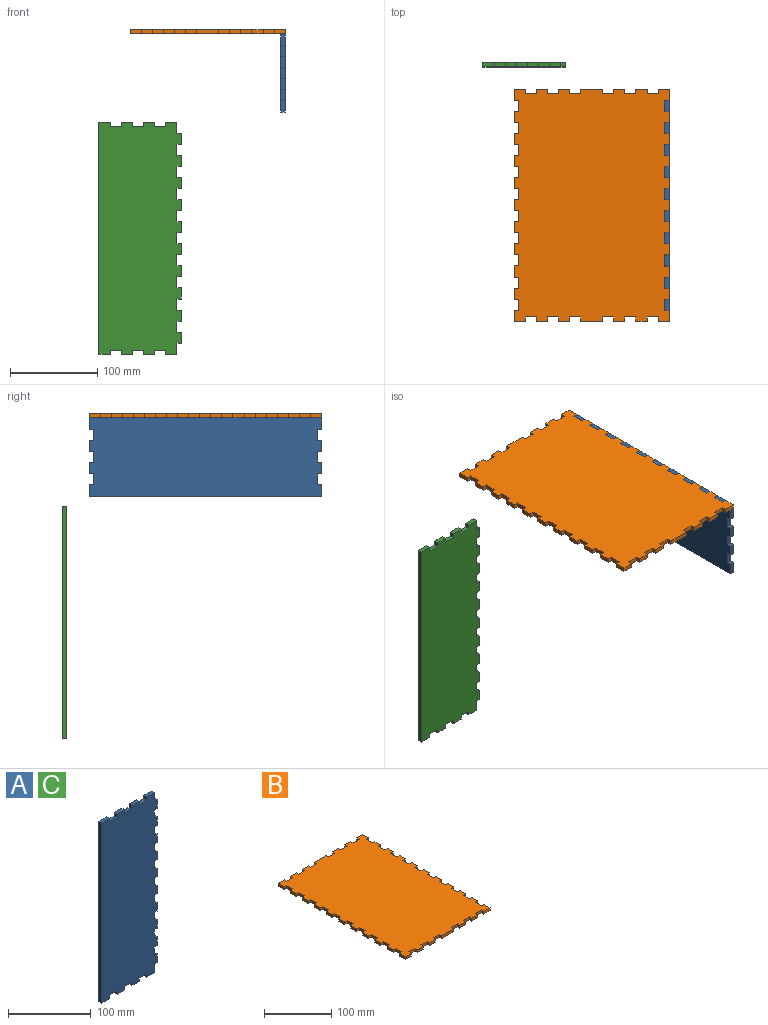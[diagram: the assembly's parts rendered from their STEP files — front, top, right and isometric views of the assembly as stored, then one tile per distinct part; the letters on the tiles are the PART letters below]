
ASSEMBLY  parts=3 mates=1
PART A: 70 faces, bbox 94.7x5x266.9 mm
  f0: plane 5x5mm, normal (0,0,-1), area 25mm2, adj f1,f67,f68,f69
  f1: plane 12.7x5mm, normal (1,0,0), area 63.5mm2, adj f0,f2,f68,f69
  f2: plane 5x5mm, normal (0,0,1), area 25mm2, adj f1,f3,f68,f69
  f3: plane 12.7x5mm, normal (1,0,0), area 63.5mm2, adj f2,f4,f68,f69
  f4: plane 5x5mm, normal (0,0,-1), area 25mm2, adj f3,f5,f68,f69
  f5: plane 12.7x5mm, normal (1,0,0), area 63.5mm2, adj f4,f6,f68,f69
  f6: plane 5x5mm, normal (0,0,1), area 25mm2, adj f5,f7,f68,f69
  f7: plane 12.7x5mm, normal (1,0,0), area 63.5mm2, adj f6,f8,f68,f69
  f8: plane 5x5mm, normal (0,0,-1), area 25mm2, adj f7,f9,f68,f69
  f9: plane 12.7x5mm, normal (1,0,0), area 63.5mm2, adj f8,f10,f68,f69
  f10: plane 5x5mm, normal (0,0,1), area 25mm2, adj f9,f11,f68,f69
  f11: plane 12.7x5mm, normal (1,0,0), area 63.5mm2, adj f10,f12,f68,f69
  f12: plane 5x5mm, normal (0,0,-1), area 25mm2, adj f11,f13,f68,f69
  f13: plane 12.7x5mm, normal (1,0,0), area 63.5mm2, adj f12,f14,f68,f69
  f14: plane 5x5mm, normal (0,0,1), area 25mm2, adj f13,f15,f68,f69
  f15: plane 12.7x5mm, normal (1,0,0), area 63.5mm2, adj f14,f16,f68,f69
  f16: plane 5x5mm, normal (0,0,-1), area 25mm2, adj f15,f17,f68,f69
  f17: plane 12.7x5mm, normal (1,0,0), area 63.5mm2, adj f16,f18,f68,f69
  f18: plane 5x5mm, normal (0,0,1), area 25mm2, adj f17,f19,f68,f69
  f19: plane 12.7x5mm, normal (1,0,0), area 63.5mm2, adj f18,f20,f68,f69
  f20: plane 5x5mm, normal (0,0,-1), area 25mm2, adj f19,f21,f68,f69
  f21: plane 12.8x5mm, normal (1,0,0), area 64mm2, adj f20,f22,f68,f69
  f22: plane 5x5mm, normal (0,0,1), area 25mm2, adj f21,f23,f68,f69
  f23: plane 12.7x5mm, normal (1,0,0), area 63.5mm2, adj f22,f24,f68,f69
  f24: plane 12.7x5mm, normal (0,0,1), area 63.5mm2, adj f23,f25,f68,f69
  f25: plane 5x5mm, normal (-1,0,0), area 25mm2, adj f24,f26,f68,f69
  f26: plane 12.7x5mm, normal (0,0,1), area 63.5mm2, adj f25,f27,f68,f69
  f27: plane 5x5mm, normal (1,0,0), area 25mm2, adj f26,f28,f68,f69
  f28: plane 12.7x5mm, normal (0,0,1), area 63.5mm2, adj f27,f29,f68,f69
  f29: plane 5x5mm, normal (-1,0,0), area 25mm2, adj f28,f30,f68,f69
  f30: plane 12.7x5mm, normal (0,0,1), area 63.5mm2, adj f29,f31,f68,f69
  f31: plane 5x5mm, normal (1,0,0), area 25mm2, adj f30,f32,f68,f69
  f32: plane 12.7x5mm, normal (0,0,1), area 63.5mm2, adj f31,f33,f68,f69
  f33: plane 5x5mm, normal (-1,0,0), area 25mm2, adj f32,f34,f68,f69
  f34: plane 12.7x5mm, normal (0,0,1), area 63.5mm2, adj f33,f35,f68,f69
  f35: plane 5x5mm, normal (1,0,0), area 25mm2, adj f34,f36,f68,f69
  f36: plane 13.49x5mm, normal (0,0,1), area 67.4mm2, adj f35,f37,f68,f69
  f37: plane 266.9x5mm, normal (-1,0,0), area 1334.5mm2, adj f36,f38,f68,f69
  f38: plane 13.49x5mm, normal (0,0,-1), area 67.4mm2, adj f37,f39,f68,f69
  f39: plane 5x5mm, normal (1,0,0), area 25mm2, adj f38,f40,f68,f69
  f40: plane 12.7x5mm, normal (0,0,-1), area 63.5mm2, adj f39,f41,f68,f69
  f41: plane 5x5mm, normal (-1,0,0), area 25mm2, adj f40,f42,f68,f69
  f42: plane 12.7x5mm, normal (0,0,-1), area 63.5mm2, adj f41,f43,f68,f69
  f43: plane 5x5mm, normal (1,0,0), area 25mm2, adj f42,f44,f68,f69
  f44: plane 12.7x5mm, normal (0,0,-1), area 63.5mm2, adj f43,f45,f68,f69
  f45: plane 5x5mm, normal (-1,0,0), area 25mm2, adj f44,f46,f68,f69
  f46: plane 12.7x5mm, normal (0,0,-1), area 63.5mm2, adj f45,f47,f68,f69
  f47: plane 5x5mm, normal (1,0,0), area 25mm2, adj f46,f48,f68,f69
  f48: plane 12.7x5mm, normal (0,0,-1), area 63.5mm2, adj f47,f49,f68,f69
  f49: plane 5x5mm, normal (-1,0,0), area 25mm2, adj f48,f50,f68,f69
  f50: plane 12.7x5mm, normal (0,0,-1), area 63.5mm2, adj f49,f51,f68,f69
  f51: plane 12.7x5mm, normal (1,0,0), area 63.5mm2, adj f50,f52,f68,f69
  f52: plane 5x5mm, normal (0,0,-1), area 25mm2, adj f51,f53,f68,f69
  f53: plane 12.8x5mm, normal (1,0,0), area 64mm2, adj f52,f54,f68,f69
  f54: plane 5x5mm, normal (0,0,1), area 25mm2, adj f53,f55,f68,f69
  f55: plane 12.7x5mm, normal (1,0,0), area 63.5mm2, adj f54,f56,f68,f69
  f56: plane 5x5mm, normal (0,0,-1), area 25mm2, adj f55,f57,f68,f69
  f57: plane 12.7x5mm, normal (1,0,0), area 63.5mm2, adj f56,f58,f68,f69
  f58: plane 5x5mm, normal (0,0,1), area 25mm2, adj f57,f59,f68,f69
  f59: plane 12.7x5mm, normal (1,0,0), area 63.5mm2, adj f58,f60,f68,f69
  f60: plane 5x5mm, normal (0,0,-1), area 25mm2, adj f59,f61,f68,f69
  f61: plane 12.7x5mm, normal (1,0,0), area 63.5mm2, adj f60,f62,f68,f69
  f62: plane 5x5mm, normal (0,0,1), area 25mm2, adj f61,f63,f68,f69
  f63: plane 12.7x5mm, normal (1,0,0), area 63.5mm2, adj f62,f64,f68,f69
  f64: plane 5x5mm, normal (0,0,-1), area 25mm2, adj f63,f65,f68,f69
  f65: plane 12.7x5mm, normal (1,0,0), area 63.5mm2, adj f64,f66,f68,f69
  f66: plane 5x5mm, normal (0,0,1), area 25mm2, adj f65,f67,f68,f69
  f67: plane 12.7x5mm, normal (1,0,0), area 63.5mm2, adj f0,f66,f68,f69
  f68: plane 266.9x94.69mm, normal (0,-1,0), area 24192.3mm2, adj f0,f1,f2,f3,f4,f5,f6,f7
  f69: plane 266.9x94.69mm, normal (0,1,0), area 24192.3mm2, adj f0,f1,f2,f3,f4,f5,f6,f7
PART B: 134 faces, bbox 177.8x266.7x5 mm
  f0: plane 12.7x5mm, normal (0,1,0), area 63.5mm2, adj f1,f131,f132,f133
  f1: plane 5x4.89mm, normal (1,0,0), area 24.4mm2, adj f0,f2,f132,f133
  f2: plane 12.7x5mm, normal (0.01,1,0), area 63.5mm2, adj f1,f3,f132,f133
  f3: plane 5x5mm, normal (-1,0,0), area 25mm2, adj f2,f4,f132,f133
  f4: plane 12.7x5mm, normal (0,1,0), area 63.5mm2, adj f3,f5,f132,f133
  f5: plane 5x5mm, normal (1,0,0), area 25mm2, adj f4,f6,f132,f133
  f6: plane 12.7x5mm, normal (0,1,0), area 63.5mm2, adj f5,f7,f132,f133
  f7: plane 12.7x5mm, normal (-1,0,0), area 63.5mm2, adj f6,f8,f132,f133
  f8: plane 5x5mm, normal (0,-1,0), area 25mm2, adj f7,f9,f132,f133
  f9: plane 12.7x5mm, normal (-1,0,0), area 63.5mm2, adj f8,f10,f132,f133
  f10: plane 5x5mm, normal (0,1,0), area 25mm2, adj f9,f11,f132,f133
  f11: plane 12.7x5mm, normal (-1,0,0), area 63.5mm2, adj f10,f12,f132,f133
  f12: plane 5x5mm, normal (0,-1,0), area 25mm2, adj f11,f13,f132,f133
  f13: plane 12.7x5mm, normal (-1,0,0), area 63.5mm2, adj f12,f14,f132,f133
  f14: plane 5x5mm, normal (0,1,0), area 25mm2, adj f13,f15,f132,f133
  f15: plane 12.7x5mm, normal (-1,0,0), area 63.5mm2, adj f14,f16,f132,f133
  f16: plane 5x5mm, normal (0,-1,0), area 25mm2, adj f15,f17,f132,f133
  f17: plane 12.7x5mm, normal (-1,0,0), area 63.5mm2, adj f16,f18,f132,f133
  f18: plane 5x5mm, normal (0,1,0), area 25mm2, adj f17,f19,f132,f133
  f19: plane 12.7x5mm, normal (-1,0,0), area 63.5mm2, adj f18,f20,f132,f133
  f20: plane 5x5mm, normal (0,-1,0), area 25mm2, adj f19,f21,f132,f133
  f21: plane 12.7x5mm, normal (-1,0,0), area 63.5mm2, adj f20,f22,f132,f133
  f22: plane 5x5mm, normal (0,1,0), area 25mm2, adj f21,f23,f132,f133
  f23: plane 12.7x5mm, normal (-1,0,0), area 63.5mm2, adj f22,f24,f132,f133
  f24: plane 5x5mm, normal (0,-1,0), area 25mm2, adj f23,f25,f132,f133
  f25: plane 12.7x5mm, normal (-1,0,0), area 63.5mm2, adj f24,f26,f132,f133
  f26: plane 5x5mm, normal (0,1,0), area 25mm2, adj f25,f27,f132,f133
  f27: plane 12.7x5mm, normal (-1,0,0), area 63.5mm2, adj f26,f28,f132,f133
  f28: plane 5x5mm, normal (0,-1,0), area 25mm2, adj f27,f29,f132,f133
  f29: plane 12.7x5mm, normal (-1,0,0), area 63.5mm2, adj f28,f30,f132,f133
  f30: plane 5x5mm, normal (0,1,0), area 25mm2, adj f29,f31,f132,f133
  f31: plane 12.7x5mm, normal (-1,0,0), area 63.5mm2, adj f30,f32,f132,f133
  f32: plane 5x5mm, normal (0,-1,0), area 25mm2, adj f31,f33,f132,f133
  f33: plane 12.7x5mm, normal (-1,0,0), area 63.5mm2, adj f32,f34,f132,f133
  f34: plane 5x5mm, normal (0,1,0), area 25mm2, adj f33,f35,f132,f133
  f35: plane 12.7x5mm, normal (-1,0,0), area 63.5mm2, adj f34,f36,f132,f133
  f36: plane 5x5mm, normal (0,-1,0), area 25mm2, adj f35,f37,f132,f133
  f37: plane 12.7x5mm, normal (-1,0,0), area 63.5mm2, adj f36,f38,f132,f133
  f38: plane 5x5mm, normal (0,1,0), area 25mm2, adj f37,f39,f132,f133
  f39: plane 12.7x5mm, normal (-1,0,0), area 63.5mm2, adj f38,f40,f132,f133
  f40: plane 5x5mm, normal (0,-1,0), area 25mm2, adj f39,f41,f132,f133
  f41: plane 12.7x5mm, normal (-1,0,0), area 63.5mm2, adj f40,f42,f132,f133
  f42: plane 5x5mm, normal (0,1,0), area 25mm2, adj f41,f43,f132,f133
  f43: plane 12.7x5mm, normal (-1,0,0), area 63.5mm2, adj f42,f44,f132,f133
  f44: plane 5x5mm, normal (0,-1,0), area 25mm2, adj f43,f45,f132,f133
  f45: plane 12.7x5mm, normal (-1,0,0), area 63.5mm2, adj f44,f46,f132,f133
  f46: plane 5x5mm, normal (0,1,0), area 25mm2, adj f45,f47,f132,f133
  f47: plane 12.7x5mm, normal (-1,0,0), area 63.5mm2, adj f46,f48,f132,f133
  f48: plane 12.7x5mm, normal (0,-1,0), area 63.5mm2, adj f47,f49,f132,f133
  f49: plane 5x5mm, normal (1,0,0), area 25mm2, adj f48,f50,f132,f133
  f50: plane 12.7x5mm, normal (0,-1,0), area 63.5mm2, adj f49,f51,f132,f133
  f51: plane 5x5mm, normal (-1,0,0), area 25mm2, adj f50,f52,f132,f133
  f52: plane 12.7x5mm, normal (0.01,-1,0), area 63.5mm2, adj f51,f53,f132,f133
  f53: plane 5x4.89mm, normal (1,0,0), area 24.4mm2, adj f52,f54,f132,f133
  f54: plane 12.7x5mm, normal (0,-1,0), area 63.5mm2, adj f53,f55,f132,f133
  f55: plane 5x5mm, normal (-1,0,0), area 25mm2, adj f54,f56,f132,f133
  f56: plane 12.7x5mm, normal (0,-1,0), area 63.5mm2, adj f55,f57,f132,f133
  f57: plane 5x5mm, normal (1,0,0), area 25mm2, adj f56,f58,f132,f133
  f58: plane 12.7x5mm, normal (0,-1,0), area 63.5mm2, adj f57,f59,f132,f133
  f59: plane 5x5mm, normal (-1,0,0), area 25mm2, adj f58,f60,f132,f133
  f60: plane 25.4x5mm, normal (0,-1,0), area 127mm2, adj f59,f61,f132,f133
  f61: plane 5x5mm, normal (1,0,0), area 25mm2, adj f60,f62,f132,f133
  f62: plane 12.7x5mm, normal (0,-1,0), area 63.5mm2, adj f61,f63,f132,f133
  f63: plane 5x5mm, normal (-1,0,0), area 25mm2, adj f62,f64,f132,f133
  f64: plane 12.7x5mm, normal (0,-1,0), area 63.5mm2, adj f63,f65,f132,f133
  f65: plane 5x5mm, normal (1,0,0), area 25mm2, adj f64,f66,f132,f133
  f66: plane 12.7x5mm, normal (0,-1,0), area 63.5mm2, adj f65,f67,f132,f133
  f67: plane 5x4.89mm, normal (-1,0,0), area 24.4mm2, adj f66,f68,f132,f133
  f68: plane 12.7x5mm, normal (-0.01,-1,0), area 63.5mm2, adj f67,f69,f132,f133
  f69: plane 5x5mm, normal (1,0,0), area 25mm2, adj f68,f70,f132,f133
  f70: plane 12.7x5mm, normal (0,-1,0), area 63.5mm2, adj f69,f71,f132,f133
  f71: plane 5x5mm, normal (-1,0,0), area 25mm2, adj f70,f72,f132,f133
  f72: plane 12.7x5mm, normal (0,-1,0), area 63.5mm2, adj f71,f73,f132,f133
  f73: plane 12.7x5mm, normal (1,0,0), area 63.5mm2, adj f72,f74,f132,f133
  f74: plane 5x5mm, normal (0,1,0), area 25mm2, adj f73,f75,f132,f133
  f75: plane 12.7x5mm, normal (1,0,0), area 63.5mm2, adj f74,f76,f132,f133
  f76: plane 5x5mm, normal (0,-1,0), area 25mm2, adj f75,f77,f132,f133
  f77: plane 12.7x5mm, normal (1,0,0), area 63.5mm2, adj f76,f78,f132,f133
  f78: plane 5x5mm, normal (0,1,0), area 25mm2, adj f77,f79,f132,f133
  f79: plane 12.7x5mm, normal (1,0,0), area 63.5mm2, adj f78,f80,f132,f133
  f80: plane 5x5mm, normal (0,-1,0), area 25mm2, adj f79,f81,f132,f133
  f81: plane 12.7x5mm, normal (1,0,0), area 63.5mm2, adj f80,f82,f132,f133
  f82: plane 5x5mm, normal (0,1,0), area 25mm2, adj f81,f83,f132,f133
  f83: plane 12.7x5mm, normal (1,0,0), area 63.5mm2, adj f82,f84,f132,f133
  f84: plane 5x5mm, normal (0,-1,0), area 25mm2, adj f83,f85,f132,f133
  f85: plane 12.7x5mm, normal (1,0,0), area 63.5mm2, adj f84,f86,f132,f133
  f86: plane 5x5mm, normal (0,1,0), area 25mm2, adj f85,f87,f132,f133
  f87: plane 12.7x5mm, normal (1,0,0), area 63.5mm2, adj f86,f88,f132,f133
  f88: plane 5x5mm, normal (0,-1,0), area 25mm2, adj f87,f89,f132,f133
  f89: plane 12.7x5mm, normal (1,0,0), area 63.5mm2, adj f88,f90,f132,f133
  f90: plane 5x5mm, normal (0,1,0), area 25mm2, adj f89,f91,f132,f133
  f91: plane 12.7x5mm, normal (1,0,0), area 63.5mm2, adj f90,f92,f132,f133
  f92: plane 5x5mm, normal (0,-1,0), area 25mm2, adj f91,f93,f132,f133
  f93: plane 12.7x5mm, normal (1,0,0), area 63.5mm2, adj f92,f94,f132,f133
  f94: plane 5x5mm, normal (0,1,0), area 25mm2, adj f93,f95,f132,f133
  f95: plane 12.7x5mm, normal (1,0,0), area 63.5mm2, adj f94,f96,f132,f133
  f96: plane 5x5mm, normal (0,-1,0), area 25mm2, adj f95,f97,f132,f133
  f97: plane 12.7x5mm, normal (1,0,0), area 63.5mm2, adj f96,f98,f132,f133
  f98: plane 5x5mm, normal (0,1,0), area 25mm2, adj f97,f99,f132,f133
  f99: plane 12.7x5mm, normal (1,0,0), area 63.5mm2, adj f98,f100,f132,f133
  f100: plane 5x5mm, normal (0,-1,0), area 25mm2, adj f99,f101,f132,f133
  f101: plane 12.7x5mm, normal (1,0,0), area 63.5mm2, adj f100,f102,f132,f133
  f102: plane 5x5mm, normal (0,1,0), area 25mm2, adj f101,f103,f132,f133
  f103: plane 12.7x5mm, normal (1,0,0), area 63.5mm2, adj f102,f104,f132,f133
  f104: plane 5x5mm, normal (0,-1,0), area 25mm2, adj f103,f105,f132,f133
  f105: plane 12.7x5mm, normal (1,0,0), area 63.5mm2, adj f104,f106,f132,f133
  f106: plane 5x5mm, normal (0,1,0), area 25mm2, adj f105,f107,f132,f133
  f107: plane 12.7x5mm, normal (1,0,0), area 63.5mm2, adj f106,f108,f132,f133
  f108: plane 5x5mm, normal (0,-1,0), area 25mm2, adj f107,f109,f132,f133
  f109: plane 12.7x5mm, normal (1,0,0), area 63.5mm2, adj f108,f110,f132,f133
  f110: plane 5x5mm, normal (0,1,0), area 25mm2, adj f109,f111,f132,f133
  f111: plane 12.7x5mm, normal (1,0,0), area 63.5mm2, adj f110,f112,f132,f133
  f112: plane 5x5mm, normal (0,-1,0), area 25mm2, adj f111,f113,f132,f133
  f113: plane 12.7x5mm, normal (1,0,0), area 63.5mm2, adj f112,f114,f132,f133
  f114: plane 12.7x5mm, normal (0,1,0), area 63.5mm2, adj f113,f115,f132,f133
  f115: plane 5x5mm, normal (-1,0,0), area 25mm2, adj f114,f116,f132,f133
  f116: plane 12.7x5mm, normal (0,1,0), area 63.5mm2, adj f115,f117,f132,f133
  f117: plane 5x5mm, normal (1,0,0), area 25mm2, adj f116,f118,f132,f133
  f118: plane 12.7x5mm, normal (-0.01,1,0), area 63.5mm2, adj f117,f119,f132,f133
  f119: plane 5x4.89mm, normal (-1,0,0), area 24.4mm2, adj f118,f120,f132,f133
  f120: plane 12.7x5mm, normal (0,1,0), area 63.5mm2, adj f119,f121,f132,f133
  f121: plane 5x5mm, normal (1,0,0), area 25mm2, adj f120,f122,f132,f133
  f122: plane 12.7x5mm, normal (0,1,0), area 63.5mm2, adj f121,f123,f132,f133
  f123: plane 5x5mm, normal (-1,0,0), area 25mm2, adj f122,f124,f132,f133
  f124: plane 12.7x5mm, normal (0,1,0), area 63.5mm2, adj f123,f125,f132,f133
  f125: plane 5x5mm, normal (1,0,0), area 25mm2, adj f124,f126,f132,f133
  f126: plane 25.4x5mm, normal (0,1,0), area 127mm2, adj f125,f127,f132,f133
  f127: plane 5x5mm, normal (-1,0,0), area 25mm2, adj f126,f128,f132,f133
  f128: plane 12.7x5mm, normal (0,1,0), area 63.5mm2, adj f127,f129,f132,f133
  f129: plane 5x5mm, normal (1,0,0), area 25mm2, adj f128,f130,f132,f133
  f130: plane 12.7x5mm, normal (0,1,0), area 63.5mm2, adj f129,f131,f132,f133
  f131: plane 5x5mm, normal (-1,0,0), area 25mm2, adj f0,f130,f132,f133
  f132: plane 266.7x177.8mm, normal (0,0,1), area 45382.7mm2, adj f0,f1,f2,f3,f4,f5,f6,f7
  f133: plane 266.7x177.8mm, normal (0,0,-1), area 45382.7mm2, adj f0,f1,f2,f3,f4,f5,f6,f7
PART C: same geometry as A
PLACE A rot(axis=(-0.58,-0.58,-0.58),120deg) t=(-270.94,-501.04,45.15)mm
PLACE B t=(-394.88,-448.51,7.42)mm
PLACE C rot(axis=(1,0,0),180deg) t=(-357.52,-297.45,-182.92)mm
MATE fastened A.f22 <-> B.f112  axis (0,1,0) through (-273.44,-336.02,9.92)mm
